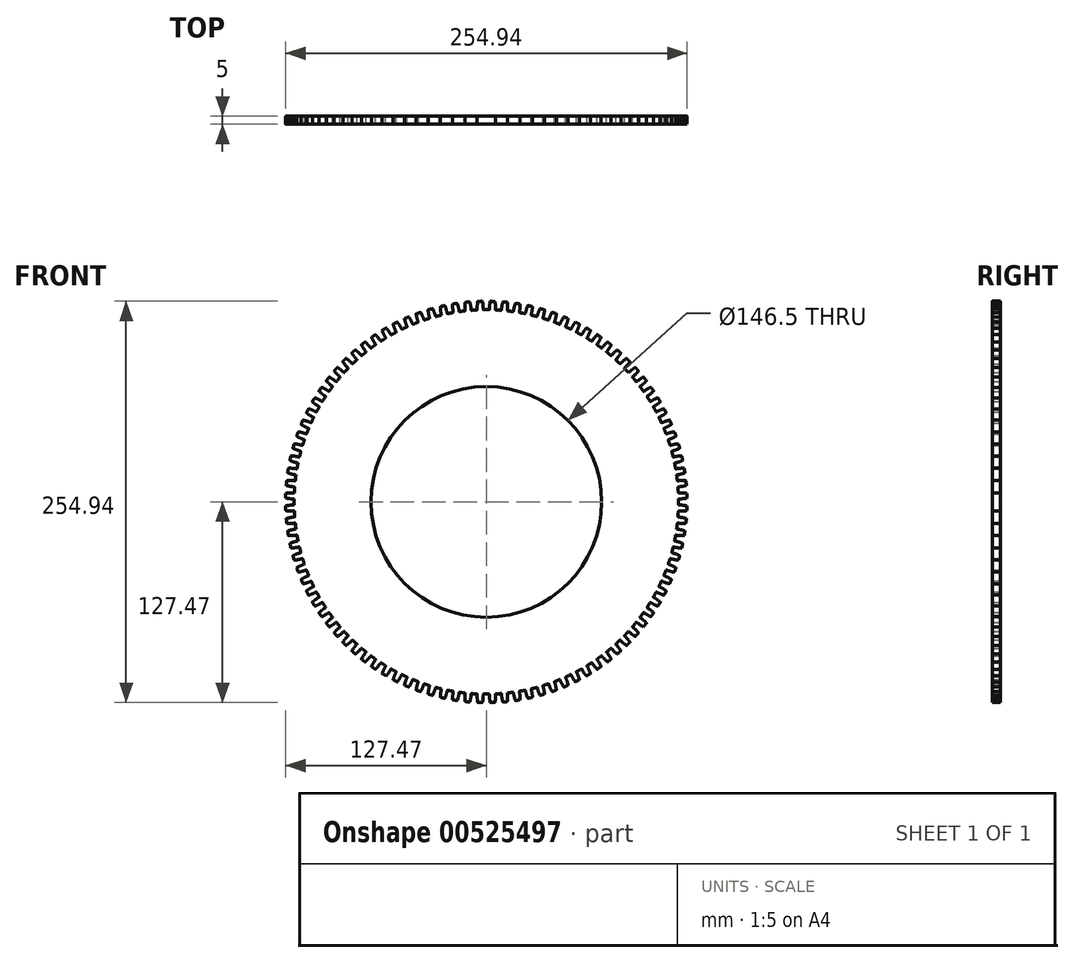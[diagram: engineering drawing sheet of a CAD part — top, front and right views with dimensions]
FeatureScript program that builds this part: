
annotation { "Feature Type Name" : "Feature", "Feature Type Description" : "" }
export const myFeature = defineFeature(function(context is Context, id is Id, definition is map)
    precondition{}
    {
        {
            assignVariable(context, id + "F0", {"name" : "d_m", "anyValue" : 250});
        }
        {
            assignVariable(context, id + "F1", {"name" : "modul", "anyValue" : 2.5});
        }
        {
            assignVariable(context, id + "F2", {"name" : "tooth", "anyValue" : getVariable(context, 'd_m') / getVariable(context, 'modul')});
        }
        {
            var Q0;
            Q0=qCreatedBy(makeId("Front.planeOp"),FACE);
            var sketch = newSketch(context, id + "F3", { "sketchPlane" : qUnion([Q0])});
            skArc(sketch, "E0", {"start": v(8, 127.25) * mm, "mid": v(6, 127.36) * mm, "end": v(4, 127.44) * mm, "construction": true});
            skArc(sketch, "E1", {"start": v(7.85, 124.75) * mm, "mid": v(3.93, 124.94) * mm, "end": v(0, 125) * mm, "construction": true});
            skArc(sketch, "E2", {"start": v(7.67, 121.84) * mm, "mid": v(3.83, 122.02) * mm, "end": v(0, 122.08) * mm, "construction": true});
            skLineSegment(sketch, "E3", {"start": v(0, 0) * mm, "end": v(0, 127.5) * mm, "construction": true});
            skLineSegment(sketch, "E4", {"start": v(0, 0) * mm, "end": v(8, 127.25) * mm, "construction": true});
            skLineSegment(sketch, "E5", {"start": v(5.6, 127.38) * mm, "end": v(0, 0) * mm, "construction": true});
            skLineSegment(sketch, "E6", {"start": v(6.4, 127.34) * mm, "end": v(0, 0) * mm, "construction": true});
            skArc(sketch, "E7", {"start": v(7.67, 121.84) * mm, "mid": v(6.9, 121.89) * mm, "end": v(6.13, 121.93) * mm});
            skLineSegment(sketch, "E8", {"start": v(4, 127.44) * mm, "end": v(0, 0) * mm, "construction": true});
            skLineSegment(sketch, "E9", {"start": v(0, 122.08) * mm, "end": v(0, 73.25) * mm});
            skArc(sketch, "E10", {"start": v(0, 73.25) * mm, "mid": v(2.3, 73.21) * mm, "end": v(4.6, 73.1) * mm});
            skLineSegment(sketch, "E11", {"start": v(4.6, 73.1) * mm, "end": v(7.67, 121.84) * mm});
            skLineSegment(sketch, "E12", {"start": v(6, 127.36) * mm, "end": v(0, 0) * mm, "construction": true});
            skArc(sketch, "E13.trimOffspring", {"start": v(4, 127.44) * mm, "mid": v(2, 127.48) * mm, "end": v(0, 127.5) * mm, "construction": true});
            skArc(sketch, "E14", {"start": v(4, 127.44) * mm, "mid": v(4.7, 127.41) * mm, "end": v(5.4, 127.39) * mm});
            skArc(sketch, "E15", {"start": v(5.76, 122.14) * mm, "mid": v(5.8, 122) * mm, "end": v(5.94, 121.94) * mm});
            skArc(sketch, "E16", {"start": v(6.13, 121.93) * mm, "mid": v(6.04, 121.93) * mm, "end": v(5.94, 121.94) * mm});
            skFitSpline(sketch, "E17", {"points": [v(5.4, 127.39) * mm, v(5.76, 122.14) * mm], "startDerivative": vector(0.6, -0.03) * mm, "endDerivative": vector(-0.39, -8.17) * mm});
            skLineSegment(sketch, "E18", {"start": v(5.8, 127.37) * mm, "end": v(0, 0) * mm, "construction": true});
            skArc(sketch, "E19.MirrorCS", {"start": v(4, 127.44) * mm, "mid": v(3.2, 127.46) * mm, "end": v(2.4, 127.48) * mm});
            skFitSpline(sketch, "E20.MirrorCS", {"points": [v(2.6, 127.47) * mm, v(1.92, 122.26) * mm], "startDerivative": vector(-0.6, 0.01) * mm, "endDerivative": vector(-0.13, -8.17) * mm});
            skArc(sketch, "E21.MirrorCS", {"start": v(1.92, 122.26) * mm, "mid": v(1.86, 122.13) * mm, "end": v(1.73, 122.07) * mm});
            skArc(sketch, "E22.MirrorCS", {"start": v(1.53, 122.07) * mm, "mid": v(1.63, 122.07) * mm, "end": v(1.73, 122.07) * mm});
            skArc(sketch, "E23.MirrorCS", {"start": v(0, 122.08) * mm, "mid": v(0.77, 122.08) * mm, "end": v(1.53, 122.07) * mm});
            skLineSegment(sketch, "E24", {"start": v(5.4, 127.39) * mm, "end": v(0, 0) * mm, "construction": true});
            skSolve(sketch);
        }
        {
            var Q0;
            Q0=makeQuery(id+"F3.imprint","IMPRINT",FACE,{"disambiguationData":[TD([[makeQuery(id+"F3.imprint","IMPRINT",EDGE,{"derivedFrom":sQuery(id+"F3.wireOp",EDGE,"E9")}),1.0]])]});
            extrude(context, id + "F4", {"entities" : qUnion([Q0]), "depth" : 5 * mm, "offsetDistance" : 25 * mm});
        }
        {
            var Q0;
            Q0=qCreatedBy(makeId("Right.planeOp"),FACE);
            var sketch = newSketch(context, id + "F5", { "sketchPlane" : qUnion([Q0])});
            skLineSegment(sketch, "E25", {"start": v(23.04, 0) * mm, "end": v(-26.85, 0) * mm});
            skSolve(sketch);
        }
        {
            var Q0;
            Q0=makeQuery(id+"F4.opExtrude","SWEPT_BODY",BODY,{"disambiguationData":[OSD([sQuery(id+"F3.wireOp",EDGE,"E9"),sQuery(id+"F3.wireOp",EDGE,"E10"),sQuery(id+"F3.wireOp",EDGE,"E11"),sQuery(id+"F3.wireOp",EDGE,"E14"),sQuery(id+"F3.wireOp",EDGE,"E7"),sQuery(id+"F3.wireOp",EDGE,"E15"),sQuery(id+"F3.wireOp",EDGE,"E16"),sQuery(id+"F3.wireOp",EDGE,"E17"),sQuery(id+"F3.wireOp",EDGE,"E19.MirrorCS"),sQuery(id+"F3.wireOp",EDGE,"E20.MirrorCS"),sQuery(id+"F3.wireOp",EDGE,"E21.MirrorCS"),sQuery(id+"F3.wireOp",EDGE,"E22.MirrorCS"),sQuery(id+"F3.wireOp",EDGE,"E23.MirrorCS")])]});
            var Q1;
            Q1=sQuery(id+"F5.wireOp",EDGE,"E25");
            circularPattern(context, id + "F6", {"operationType" : NewBodyOperationType.ADD, "entities" : qUnion([Q0]), "axis" : qUnion([Q1]), "angle" : 360 * degree, "instanceCount" : getVariable(context, 'tooth'), "equalSpace" : true});
        }
    });
